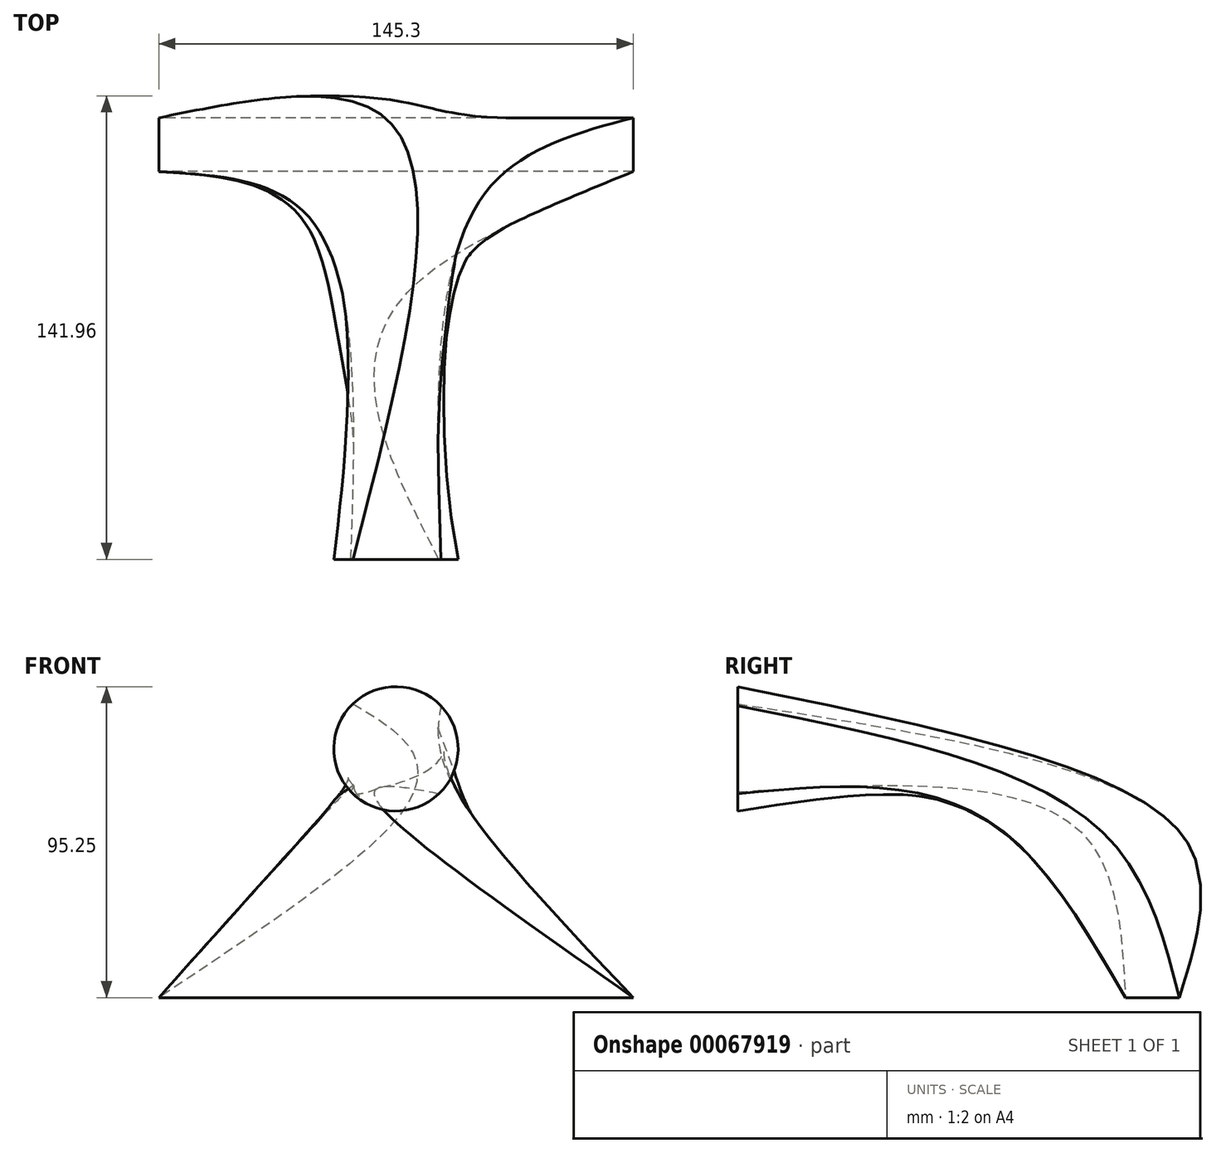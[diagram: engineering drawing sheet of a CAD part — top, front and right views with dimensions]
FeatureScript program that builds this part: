
annotation { "Feature Type Name" : "Feature", "Feature Type Description" : "" }
export const myFeature = defineFeature(function(context is Context, id is Id, definition is map)
    precondition{}
    {
        {
            var Q0;
            Q0=qCreatedBy(makeId("Top.planeOp"),FACE);
            var sketch = newSketch(context, id + "F0", { "sketchPlane" : qUnion([Q0])});
            skLineSegment(sketch, "E0.rect.bottom", {"start": v(72.65, 118.75) * mm, "end": v(-72.65, 118.75) * mm});
            skLineSegment(sketch, "E0.rect.top", {"start": v(72.65, 135.25) * mm, "end": v(-72.65, 135.25) * mm});
            skLineSegment(sketch, "E0.rect.left", {"start": v(72.65, 118.75) * mm, "end": v(72.65, 135.25) * mm});
            skLineSegment(sketch, "E0.rect.right", {"start": v(-72.65, 118.75) * mm, "end": v(-72.65, 135.25) * mm});
            skPoint(sketch, "E0.rect.middle", {"position": v(0, 127) * mm});
            skLineSegment(sketch, "E1", {"start": v(0, 0) * mm, "end": v(0, 127) * mm, "construction": true});
            skSolve(sketch);
        }
        {
            var Q0;
            Q0=qCreatedBy(makeId("Front.planeOp"),FACE);
            var sketch = newSketch(context, id + "F1", { "sketchPlane" : qUnion([Q0])});
            skLineSegment(sketch, "E2", {"start": v(0, 0) * mm, "end": v(0, 76.2) * mm, "construction": true});
            skCircle(sketch, "E3", {"center": v(0, 76.2) * mm, "radius": 19.05 * mm});
            skSolve(sketch);
        }
        {
            var Q0;
            Q0=qCreatedBy(makeId("Top.planeOp"),FACE);
            cPlane(context, id + "F2", {"entities" : qUnion([Q0]), "cplaneType" : CPlaneType.OFFSET, "offset" : 50.8 * mm, "width" : 152.4 * mm, "height" : 152.4 * mm});
        }
        {
            var Q0;
            Q0=qCreatedBy(id+"F2.planeOp",FACE);
            var sketch = newSketch(context, id + "F3", { "sketchPlane" : qUnion([Q0])});
            skCircle(sketch, "E4", {"center": v(0, 108.35) * mm, "radius": 27.08 * mm});
            skSolve(sketch);
        }
        {
            var Q0;
            Q0=makeQuery(id+"F1.imprint","IMPRINT",FACE,{"disambiguationData":[TD([[makeQuery(id+"F1.imprint","IMPRINT",EDGE,{"derivedFrom":sQuery(id+"F1.wireOp",EDGE,"E3")}),1.0]])]});
            var Q1;
            Q1=makeQuery(id+"F3.imprint","IMPRINT",FACE,{"disambiguationData":[TD([[makeQuery(id+"F3.imprint","IMPRINT",EDGE,{"derivedFrom":sQuery(id+"F3.wireOp",EDGE,"E4")}),1.0]])]});
            var Q2;
            Q2=makeQuery(id+"F0.imprint","IMPRINT",FACE,{"disambiguationData":[TD([[makeQuery(id+"F0.imprint","IMPRINT",EDGE,{"derivedFrom":sQuery(id+"F0.wireOp",EDGE,"E0.rect.bottom")}),-1.0]])]});
            loft(context, id + "F4", {"sheetProfilesArray" : [{ "sheetProfileEntities" : qUnion([Q0]) }, { "sheetProfileEntities" : qUnion([Q1]) }, { "sheetProfileEntities" : qUnion([Q2]) }]});
        }
    });
